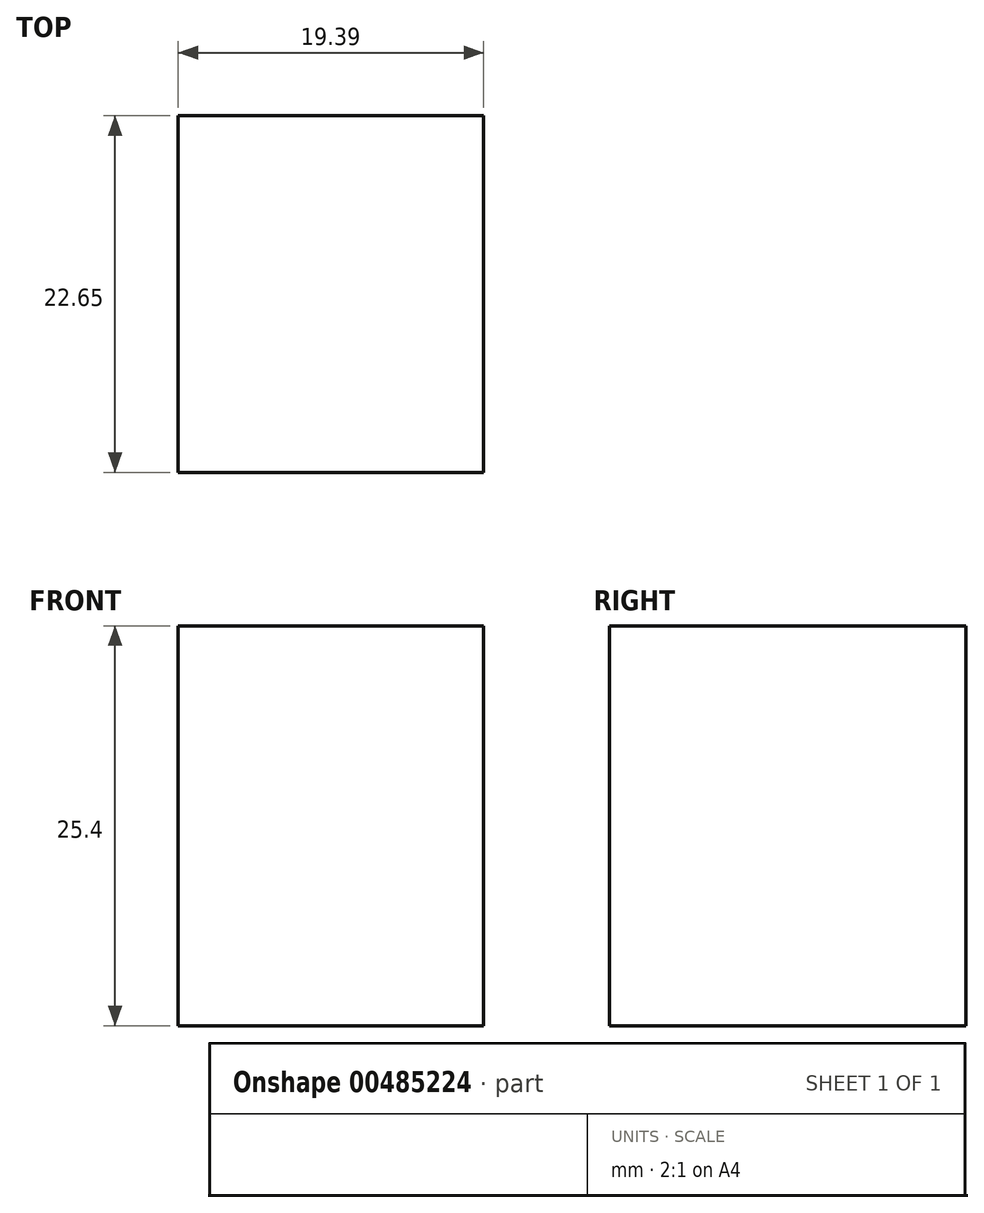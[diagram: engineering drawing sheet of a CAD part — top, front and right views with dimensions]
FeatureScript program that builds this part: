
annotation { "Feature Type Name" : "Feature", "Feature Type Description" : "" }
export const myFeature = defineFeature(function(context is Context, id is Id, definition is map)
    precondition{}
    {
        {
            var Q0;
            Q0=qCreatedBy(makeId("Top.planeOp"),FACE);
            var sketch = newSketch(context, id + "F0", { "sketchPlane" : qUnion([Q0])});
            skLineSegment(sketch, "E0.bottom", {"start": v(-0.13, -16.55) * mm, "end": v(19.26, -16.55) * mm});
            skLineSegment(sketch, "E0.top", {"start": v(-0.13, 6.1) * mm, "end": v(19.26, 6.1) * mm});
            skLineSegment(sketch, "E0.left", {"start": v(-0.13, -16.55) * mm, "end": v(-0.13, 6.1) * mm});
            skLineSegment(sketch, "E0.right", {"start": v(19.26, -16.55) * mm, "end": v(19.26, 6.1) * mm});
            skSolve(sketch);
        }
        {
            var Q0;
            Q0=makeQuery(id+"F0.imprint","IMPRINT",FACE,{"disambiguationData":[TD([[makeQuery(id+"F0.imprint","IMPRINT",EDGE,{"derivedFrom":sQuery(id+"F0.wireOp",EDGE,"E0.bottom")}),1.0]])]});
            extrude(context, id + "F1", {"entities" : qUnion([Q0]), "depth" : 25.4 * mm});
        }
    });
